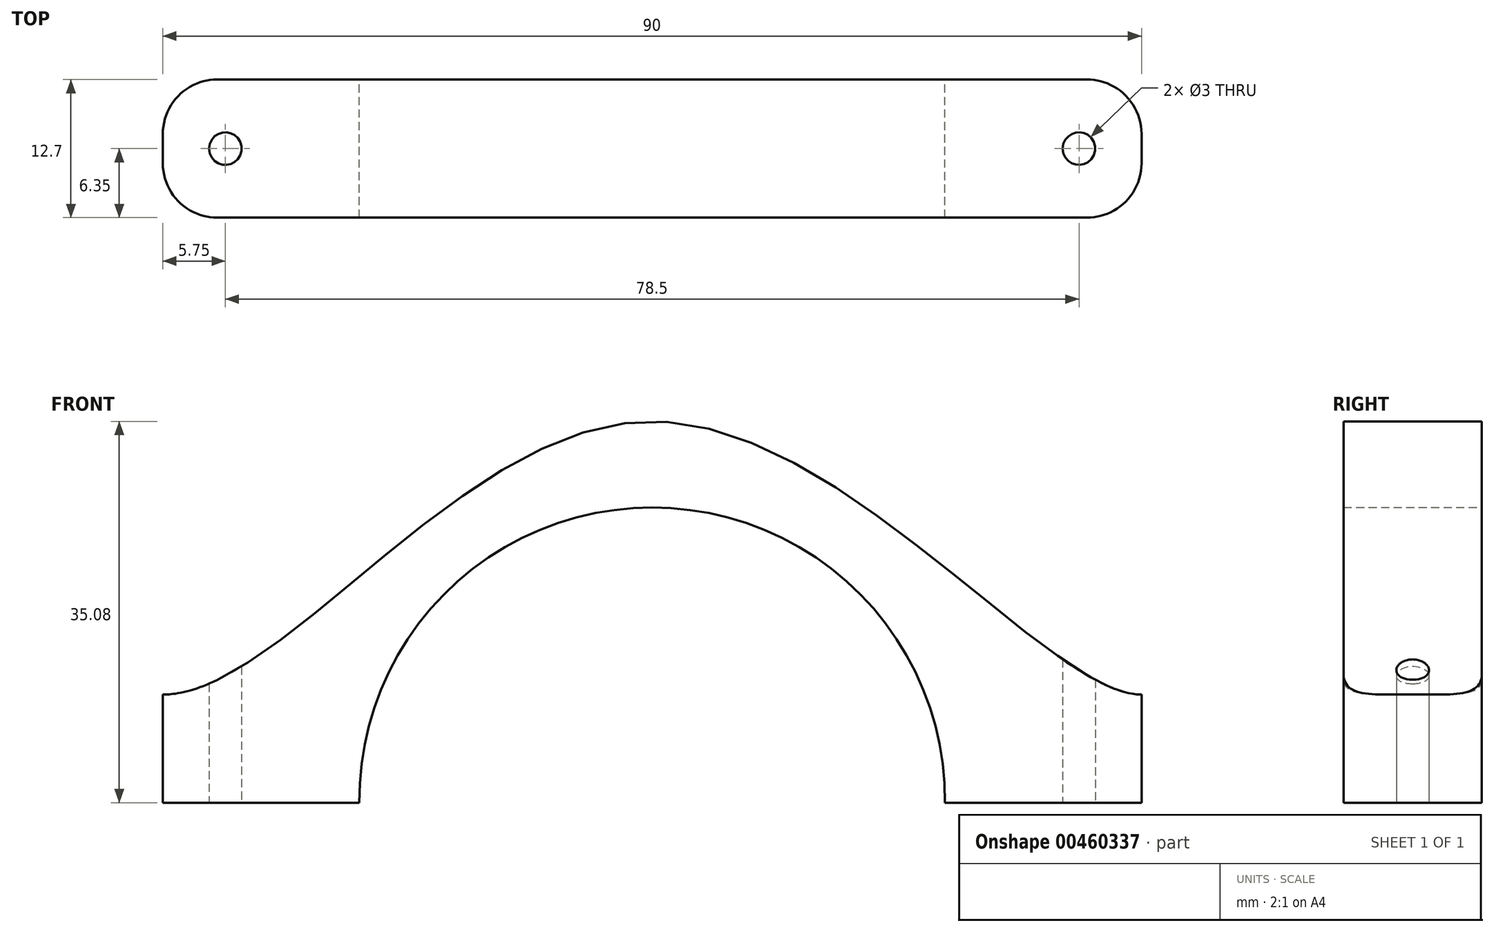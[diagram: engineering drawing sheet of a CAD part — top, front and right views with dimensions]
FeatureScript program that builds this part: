
annotation { "Feature Type Name" : "Feature", "Feature Type Description" : "" }
export const myFeature = defineFeature(function(context is Context, id is Id, definition is map)
    precondition{}
    {
        {
            var Q0;
            Q0=qCreatedBy(makeId("Front.planeOp"),FACE);
            var sketch = newSketch(context, id + "F0", { "sketchPlane" : qUnion([Q0])});
            skLineSegment(sketch, "E0.bottom", {"start": v(45, -0.23) * mm, "end": v(26.92, -0.23) * mm});
            skLineSegment(sketch, "E0.top", {"start": v(45, 9.72) * mm, "end": v(25.11, 9.72) * mm});
            skLineSegment(sketch, "E0.left", {"start": v(45, -0.23) * mm, "end": v(45, 9.72) * mm});
            skLineSegment(sketch, "E0.right", {"start": v(-45, -0.23) * mm, "end": v(-45, 9.72) * mm});
            skPoint(sketch, "E0.middle", {"position": v(0, 4.74) * mm});
            skFitSpline(sketch, "E1", {"points": [v(-45, 9.72) * mm, v(0, 34.85) * mm, v(45, 9.72) * mm], "startDerivative": vector(67.4, 0) * mm, "endDerivative": vector(52.08, 0) * mm});
            skArc(sketch, "E2", {"start": v(26.92, -0.23) * mm, "mid": v(0, 26.93) * mm, "end": v(-26.92, -0.23) * mm});
            skLineSegment(sketch, "E3.trimOffspring", {"start": v(-25.11, 9.72) * mm, "end": v(-45, 9.72) * mm});
            skLineSegment(sketch, "E4.trimOffspring", {"start": v(-26.92, -0.23) * mm, "end": v(-45, -0.23) * mm});
            skSolve(sketch);
        }
        {
            var Q0;
            Q0=qSketchRegion(id+"F0",true);
            var Q1;
            Q1=qSketchRegion(id+"F3",true);
            extrude(context, id + "F1", {"entities" : qUnion([Q0, Q1]), "depth" : 12.7 * mm});
        }
        {
            var Q0;
            Q0=makeQuery(id+"F1.opExtrude","CAP_EDGE",EDGE,{"disambiguationData":[OSD([sQuery(id+"F0.wireOp",EDGE,"E0.right")])],"isStart":false});
            var Q1;
            Q1=makeQuery(id+"F1.opExtrude","CAP_EDGE",EDGE,{"disambiguationData":[OSD([sQuery(id+"F0.wireOp",EDGE,"E0.right")])],"isStart":true});
            var Q2;
            Q2=makeQuery(id+"F1.opExtrude","CAP_EDGE",EDGE,{"disambiguationData":[OSD([sQuery(id+"F0.wireOp",EDGE,"E0.left")])],"isStart":false});
            var Q3;
            Q3=makeQuery(id+"F1.opExtrude","CAP_EDGE",EDGE,{"disambiguationData":[OSD([sQuery(id+"F0.wireOp",EDGE,"E0.left")])],"isStart":true});
            fillet(context, id + "F2", {"entities" : qUnion([Q0, Q1, Q2, Q3]), "radius" : 5 * mm, "tangentPropagation" : true, "allowEdgeOverflow" : false});
        }
        {
            var Q0;
            Q0=qCreatedBy(makeId("Top.planeOp"),FACE);
            var sketch = newSketch(context, id + "F3", { "sketchPlane" : qUnion([Q0])});
            skCircle(sketch, "E5", {"center": v(-39.25, -6.35) * mm, "radius": 1.5 * mm});
            skCircle(sketch, "E6", {"center": v(39.25, -6.35) * mm, "radius": 1.5 * mm});
            skSolve(sketch);
        }
        {
            var Q0;
            Q0=qSketchRegion(id+"F3",true);
            extrude(context, id + "F4", {"entities" : qUnion([Q0]), "operationType" : NewBodyOperationType.REMOVE, "endBound" : BoundingType.SYMMETRIC, "depth" : 30.2 * mm});
        }
    });
